# Revit family: FP_Revit_18_OS24NDBB1_Steam_Oven_90000816A
name_source: partatom
category: Specialty Equipment
revit_build: Autodesk Revit 2018 (Build: 20170223_1515(x64)
units: mm (PartAtom-declared; Revit-internal decimal feet)

## family parameters
Always vertical = Yes
Cut with Voids When Loaded = Yes
OmniClass Number = 23.40.40.14.17.31
OmniClass Title = Small Specialized Cooking Equipment
Part Type = Normal
Room Calculation Point = No
Round Connector Dimension = Use Diameter
Shared = No
Work Plane-Based = No

## types (1)
- OS24NDBB1
    Cavity - Depth = 560 mm  [stored 1.83727 ft]
    Cavity - Height = 460 mm
    Cavity - Width = 560 mm  [stored 1.83727 ft]
    Chassis - Depth = 540 mm  [stored 1.77165 ft]
    Chassis - Height = 446 mm
    Chassis - Width = 556 mm  [stored 1.82415 ft]
    Connector Description - Electrical = 208 V or 240 V, 60 Hz, 10.8 or 12.5 A
    Description = 24" Steam Oven
    Manufacturer = Fisher & Paykel Appliances
    Material - Body = Fisher & Paykel - Grey
    Material - Glass = Fisher & Paykel - Glass, Black
    Material - Handle = Fisher & Paykel - Aluminium, Dark
    Material - Structure = Fisher & Paykel - Black
    Material - Trim = Fisher & Paykel - Aluminium, Dark
    Model = OS24NDBB1
    Product - Depth = 562 mm
    Product - Height = 458 mm
    Product - Width = 596 mm
    URL = www.fisherpaykel.com
    Visibility - Clearance Required = Yes

note: [stored X ft] marks values corroborated as IEEE doubles in the binary element streams (Revit-internal decimal feet)

## geometry (parser evidence)
native form markers: Sweep x6
no freeform markers — native parametric forms only
